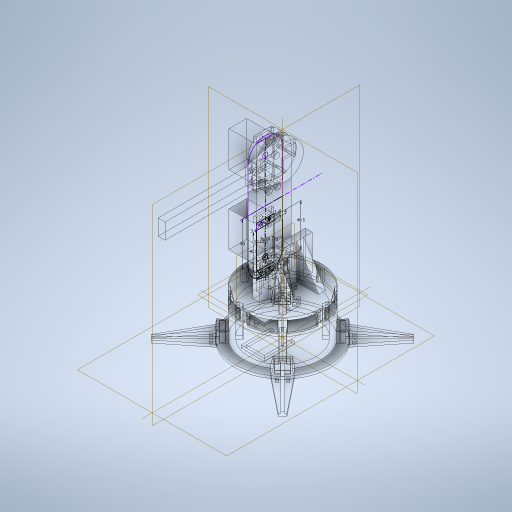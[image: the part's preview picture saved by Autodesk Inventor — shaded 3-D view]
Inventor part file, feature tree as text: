
AUTODESK INVENTOR PART (.ipt)
format: ipt  version: 2023 (Build 270158000, 158)  size: 1,345,536 bytes
history: native  units: in
note: dims shown in document units (in); Inventor stores cm internally (conversion verified against a paired STEP export)
features: extrude x28, sketch x19, other x9, move_body x4, imported_body x2, plane x2, boolean_combine x2, pattern_circular x1, revolve x1
ambient origin geometry x8: Origin, YZ Plane, XZ Plane, XY Plane, X Axis, Y Axis, Z Axis, Center Point
bodies: Solid1 (feature_tree), Solid13 (feature_tree)
feature tree (68):
  imported_body  "base"
  sketch  "Sketch1"  dims[d0=2.9921in d1=3.4646in]
  other  "Repaired Geometry1"
  extrude  "Extrusion1"  Depth=3.4646in
  extrude  "Extrusion2"  Depth=1.5748in TaperAngle=360.0deg
  extrude  "Extrusion3"  Depth=1.2598in TaperAngle=0.0deg
  extrude  "Extrusion4"  Depth=1.2205in
  extrude  "Extrusion5"  Depth=0.1181in
  sketch  "Sketch6"  dims[d3=1.2598in d6=1.5748in d8=360.0deg]
  extrude  "Extrusion7"  Depth=0.3937in
  extrude  "Extrusion9"  Depth=3.937in
  extrude  "Extrusion10"  Depth=0.0787in
  pattern_circular  "Circular Pattern1"  Count=4 Angle=360.0deg
  extrude  "base hole"  Depth=0.4724in
  extrude  "Extrusion12"  Depth=0.1274in
  plane  "Work Plane1"
  extrude  "Extrusion13"  Depth=0.1969in
  extrude  "Extrusion14"  Depth=0.0098in
  extrude  "Extrusion15"  Depth=0.1916in
  extrude  "Extrusion16"  Depth=0.1181in
  plane  "Work Plane2"
  sketch  "Sketch14"  dims[d30=0.1181in]
  extrude  "Extrusion17"  Depth=2.1654in
  extrude  "Extrusion18"  Depth=2.1358in
  extrude  "Extrusion19"  Depth=0.0787in
  extrude  "Extrusion20"  Depth=0.1181in
  extrude  "Extrusion21"  Depth=0.1181in
  extrude  "Extrusion22"  Depth=0.2756in
  extrude  "Extrusion23"  Depth=0.1181in
  boolean_combine  "Combine1"
  move_body  "Move Body1"
  move_body  "Move Body2"
  move_body  "Move Body3"
  boolean_combine  "Combine2"
  sketch  "Sketch19"  dims[d72=0.1969in d73=0.0098in]
  extrude  "Extrusion24"  Depth=0.1181in
  sketch  "Sketch20"  dims[d77=0.1181in d78=0.1916in]
  extrude  "Extrusion25"  Depth=0.2756in
  extrude  "Extrusion26"  Depth=1.5748in TaperAngle=360.0deg
  extrude  "Extrusion28"  Depth=0.4724in TaperAngle=0.0deg
  extrude  "Extrusion29"  Depth=0.1181in TaperAngle=0.0deg
  move_body  "Move Body4"
  extrude  "Extrusion30"  Depth=0.0787in
  revolve  "Revolution1"  [1 undecoded]
  extrude  "Extrusion31"  Depth=1.5748in TaperAngle=360.0deg
  other  "motor mount"
  other  "base extention legs"
  sketch  "Sketch7"  dims[d10=4.252in d11=1.2598in d12=0.0in]
  sketch  "Sketch8"  dims[d13=0.1181in d14=0.0in d16=1.2205in]
  sketch  "Sketch9"  dims[d18=0.4035in d19=0.1181in]
  other  "base top"
  sketch  "Sketch10"  dims[d20=0.1181in d21=0.0in d22=0.3937in]
  other  "rotate base"
  sketch  "Sketch12"  dims[d23=3.937in d24=0.0in d25=0.2405in]
  sketch  "Sketch13"  dims[d26=0.1374in d29=0.0787in]
  other  "servo motor"
  sketch  "Sketch15"  dims[d31=0.1969in d32=1.5748in d34=360.0deg]
  sketch  "Sketch16"  dims[d36=0.4724in d37=0.0in d66=0.3071in]
  sketch  "Sketch17"  dims[d67=0.3071in d69=0.1274in]
  sketch  "Sketch18"  dims[d70=0.1969in d71=0.1969in]
  other  "link1"
  imported_body  "Base1"
  other  "link2"
  sketch  "Sketch21"  dims[d79=0.1916in d80=0.1181in]
  sketch  "Sketch22"  dims[d81=2.1654in d82=0.1374in]
  sketch  "Sketch23"  dims[d83=0.2405in d84=2.1358in]
  sketch  "Sketch24"  dims[d85=0.0787in d86=0.0787in d87=0.1181in d88=0.1181in d89=0.2756in d90=0.1181in d91=0.1181in d92=0.2756in d93=1.5748in d95=360.0deg d97=0.4724in d98=0.0in d101=0.1181in d102=0.0in d103=0.0787in d104=0.1181in d105=0.0in d106=1.5748in d107=360.0deg d109=0.0866in d112=1.4173in d113=1.5748in d115=360.0deg d117=0.5906in d118=0.0in d119=0.374in d120=0.187in d121=0.1476in d122=0.1476in d123=1.9094in d124=1.9094in d125=0.374in d126=0.1378in d127=0.1378in d128=0.1378in d129=0.1378in d130=3.4646in d131=1.5748in d133=360.0deg d135=1.5748in d137=360.0deg d139=0.1181in d140=0.0in d141=0.8071in d142=1.5945in d143=0.4035in d144=0.4035in d145=0.1575in d146=0.2756in d147=3.4646in d148=45.0deg d149=0.4134in d150=0.0866in d151=1.5748in d153=360.0deg d155=0.1181in d156=0.0in d157=0.315in d160=2.3622in d161=1.1811in d163=0.1575in d164=1.5748in d165=0.0in d166=0.9843in d167=1.5748in d168=0.0in d169=0.315in d171=0.9843in d172=0.8268in d173=0.0in d174=0.0866in d175=1.5748in d177=360.0deg d179=0.315in d180=0.0in d181=0.6299in d183=1.5945in d184=0.2756in d186=0.0984in d187=0.0in d188=1.2205in d189=0.0in d190=0.3937in d191=0.0in d195=0.5413in d197=0.3986in d198=0.3986in d199=0.2756in d200=0.6594in d202=0.2362in d204=1.5945in d205=0.2756in d206=0.6053in d207=0.6053in d208=0.2756in d209=0.6594in d210=0.2362in d211=0.0891in d212=0.1378in d213=0.0in d214=1.4567in d215=0.3937in d216=1.4567in d217=0.3937in d218=0.0866in d219=0.4134in d220=1.5748in d222=360.0deg d224=0.0984in d225=0.0in d227=1.9094in d228=0.1575in d229=0.1575in d230=0.7972in d231=0.187in d232=0.187in d233=0.187in d234=0.187in d235=0.1339in d236=0.1339in d237=0.1339in d238=0.1339in d240=0.1181in d242=0.0984in d243=0.0in d245=0.3937in d246=0.0in d247=180.0deg d248=180.0deg d249=0.7874in d250=0.0in d251=0.0in d255=1.9685in d256=0.315in d257=0.0in d258=4.3307in d259=11.4173in d262=0.1181in d263=0.1181in d264=0.2362in d265=0.2362in d266=0.2362in d267=0.2362in d268=1.4961in d270=0.1181in d271=0.1181in d272=0.1181in d273=0.1181in d274=0.1181in d275=0.1181in d276=0.315in d277=0.0in d278=0.0984in d279=0.0in d282=0.2835in d283=0.0in d284=3.937in d285=0.0in d286=0.0in d287=0.2362in d288=0.0in d289=0.0344in d290=0.0787in d291=3.1496in d293=360.0deg d295=0.5118in d296=0.0in d297=1.5354in d298=0.0103in d299=3.1496in d301=360.0deg d303=90.0deg d304=0.4724in d305=0.7874in d306=0.0in d307=0.2362in d308=0.2283in d309=0.0in]
  other  "servo 2"
note: 1 required parameter value undecoded (feature->parameter linkage not recoverable at this tier; creation-order binding heuristic only, values carry confidence <= 0.55)
